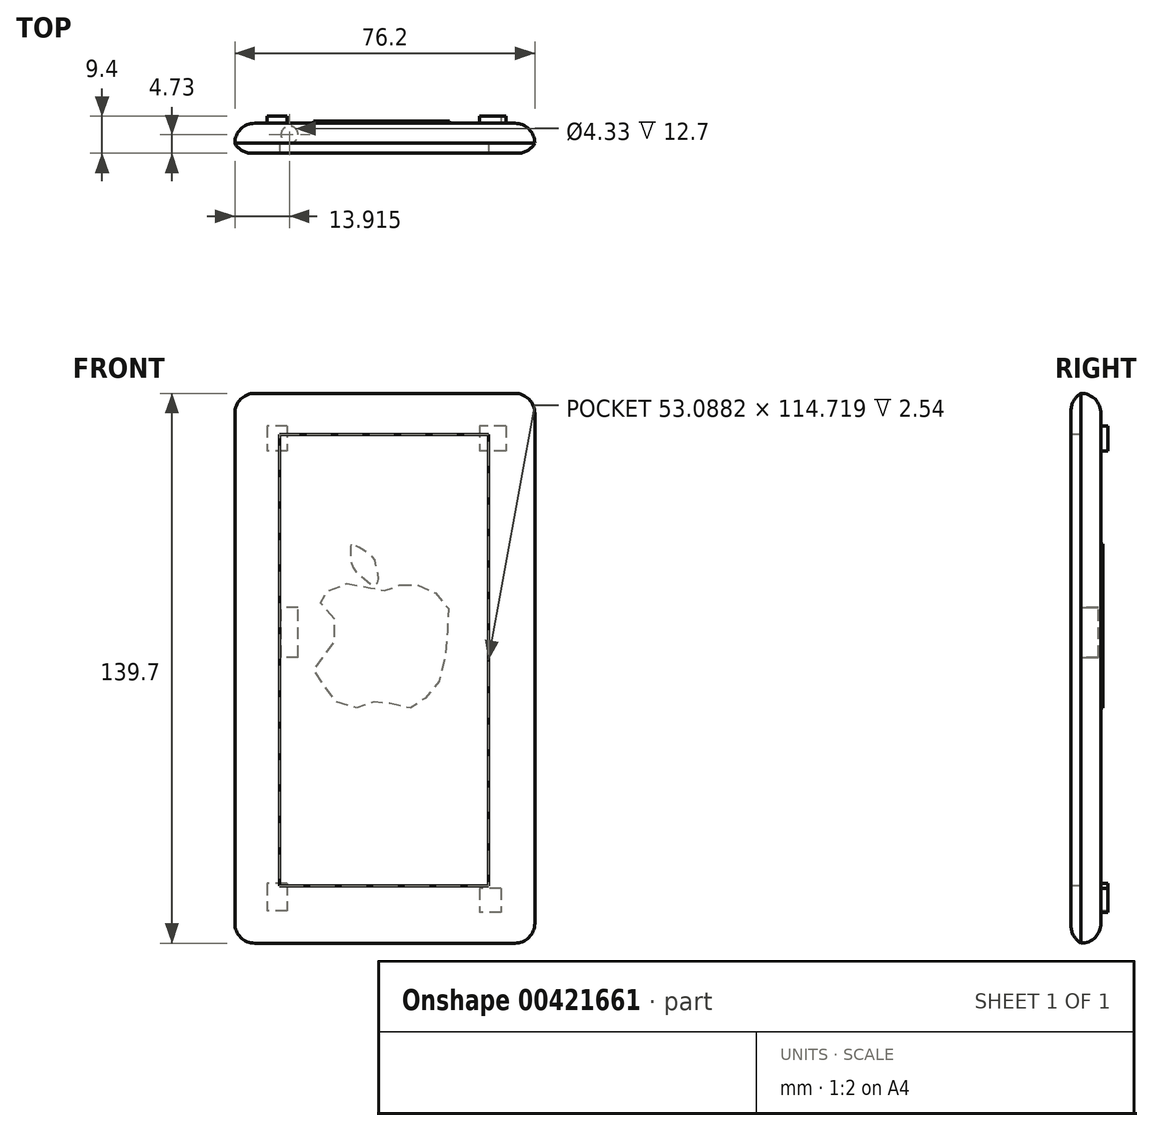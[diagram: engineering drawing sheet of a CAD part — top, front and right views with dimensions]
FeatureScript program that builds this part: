
annotation { "Feature Type Name" : "Feature", "Feature Type Description" : "" }
export const myFeature = defineFeature(function(context is Context, id is Id, definition is map)
    precondition{}
    {
        {
            var Q0;
            Q0=qCreatedBy(makeId("Front.planeOp"),FACE);
            var sketch = newSketch(context, id + "F0", { "sketchPlane" : qUnion([Q0])});
            skLineSegment(sketch, "E0.bottom", {"start": v(-44.86, 54.34) * mm, "end": v(31.34, 54.34) * mm});
            skLineSegment(sketch, "E0.top", {"start": v(-44.86, -85.36) * mm, "end": v(31.34, -85.36) * mm});
            skLineSegment(sketch, "E0.left", {"start": v(-44.86, 54.34) * mm, "end": v(-44.86, -85.36) * mm});
            skLineSegment(sketch, "E0.right", {"start": v(31.34, 54.34) * mm, "end": v(31.34, -85.36) * mm});
            skSolve(sketch);
        }
        {
            var Q0;
            Q0=makeQuery(id+"F0.imprint","IMPRINT",FACE,{"disambiguationData":[TD([[makeQuery(id+"F0.imprint","IMPRINT",EDGE,{"derivedFrom":sQuery(id+"F0.wireOp",EDGE,"E0.bottom")}),-1.0]])]});
            extrude(context, id + "F1", {"entities" : qUnion([Q0]), "depth" : 7.62 * mm});
        }
        {
            var Q0;
            Q0=makeQuery(id+"F1.opExtrude","SWEPT_EDGE",EDGE,{"disambiguationData":[OSD([sQuery(id+"F0.wireOp",EDGE,"E0.bottom"),sQuery(id+"F0.wireOp",EDGE,"E0.left")])]});
            fillet(context, id + "F2", {"entities" : qUnion([Q0]), "radius" : 5.08 * mm, "tangentPropagation" : true, "allowEdgeOverflow" : false});
        }
        {
            var Q0;
            Q0=makeQuery(id+"F1.opExtrude","SWEPT_EDGE",EDGE,{"disambiguationData":[OSD([sQuery(id+"F0.wireOp",EDGE,"E0.top"),sQuery(id+"F0.wireOp",EDGE,"E0.right")])]});
            fillet(context, id + "F3", {"entities" : qUnion([Q0]), "radius" : 5.08 * mm, "tangentPropagation" : true, "allowEdgeOverflow" : false});
        }
        {
            var Q0;
            Q0=makeQuery(id+"F1.opExtrude","SWEPT_EDGE",EDGE,{"disambiguationData":[OSD([sQuery(id+"F0.wireOp",EDGE,"E0.bottom"),sQuery(id+"F0.wireOp",EDGE,"E0.right")])]});
            fillet(context, id + "F4", {"entities" : qUnion([Q0]), "radius" : 5.08 * mm, "tangentPropagation" : true, "allowEdgeOverflow" : false});
        }
        {
            var Q0;
            Q0=makeQuery(id+"F1.opExtrude","SWEPT_EDGE",EDGE,{"disambiguationData":[OSD([sQuery(id+"F0.wireOp",EDGE,"E0.top"),sQuery(id+"F0.wireOp",EDGE,"E0.left")])]});
            fillet(context, id + "F5", {"entities" : qUnion([Q0]), "radius" : 5.08 * mm, "tangentPropagation" : true, "allowEdgeOverflow" : false});
        }
        {
            var Q0;
            Q0=makeQuery(id+"F1.opExtrude","CAP_EDGE",EDGE,{"disambiguationData":[OSD([sQuery(id+"F0.wireOp",EDGE,"E0.left")])],"isStart":true});
            fillet(context, id + "F6", {"entities" : qUnion([Q0]), "radius" : 5.08 * mm, "tangentPropagation" : true, "allowEdgeOverflow" : false});
        }
        {
            var Q0;
            Q0=makeQuery(id+"F1.opExtrude","CAP_FACE",FACE,{"disambiguationData":[OSD([sQuery(id+"F0.wireOp",EDGE,"E0.bottom"),sQuery(id+"F0.wireOp",EDGE,"E0.top"),sQuery(id+"F0.wireOp",EDGE,"E0.left"),sQuery(id+"F0.wireOp",EDGE,"E0.right")])],"isStart":false});
            var sketch = newSketch(context, id + "F7", { "sketchPlane" : qUnion([Q0])});
            skLineSegment(sketch, "E1.bottom", {"start": v(-33.56, 43.93) * mm, "end": v(19.53, 43.93) * mm});
            skLineSegment(sketch, "E1.top", {"start": v(-33.56, -70.79) * mm, "end": v(19.53, -70.79) * mm});
            skLineSegment(sketch, "E1.left", {"start": v(-33.56, 43.93) * mm, "end": v(-33.56, -70.79) * mm});
            skLineSegment(sketch, "E1.right", {"start": v(19.53, 43.93) * mm, "end": v(19.53, -70.79) * mm});
            skSolve(sketch);
        }
        {
            var Q0;
            Q0=makeQuery(id+"F1.opExtrude","CAP_FACE",FACE,{"disambiguationData":[OSD([sQuery(id+"F0.wireOp",EDGE,"E0.bottom"),sQuery(id+"F0.wireOp",EDGE,"E0.top"),sQuery(id+"F0.wireOp",EDGE,"E0.left"),sQuery(id+"F0.wireOp",EDGE,"E0.right")])],"isStart":true});
            var sketch = newSketch(context, id + "F8", { "sketchPlane" : qUnion([Q0])});
            skLineSegment(sketch, "E2.bottom", {"start": v(-24, 46.07) * mm, "end": v(-17.29, 46.07) * mm});
            skLineSegment(sketch, "E2.top", {"start": v(-24, 39.66) * mm, "end": v(-17.29, 39.66) * mm});
            skLineSegment(sketch, "E2.left", {"start": v(-24, 46.07) * mm, "end": v(-24, 39.66) * mm});
            skLineSegment(sketch, "E2.right", {"start": v(-17.29, 46.07) * mm, "end": v(-17.29, 39.66) * mm});
            skLineSegment(sketch, "E3.bottom", {"start": v(31.53, 46.07) * mm, "end": v(36.71, 46.07) * mm});
            skLineSegment(sketch, "E3.top", {"start": v(31.53, 39.66) * mm, "end": v(36.71, 39.66) * mm});
            skLineSegment(sketch, "E3.left", {"start": v(31.53, 46.07) * mm, "end": v(31.53, 39.66) * mm});
            skLineSegment(sketch, "E3.right", {"start": v(36.71, 46.07) * mm, "end": v(36.71, 39.66) * mm});
            skLineSegment(sketch, "E4.bottom", {"start": v(-22.78, -71.4) * mm, "end": v(-17.29, -71.4) * mm});
            skLineSegment(sketch, "E4.top", {"start": v(-22.78, -77.5) * mm, "end": v(-17.29, -77.5) * mm});
            skLineSegment(sketch, "E4.left", {"start": v(-22.78, -71.4) * mm, "end": v(-22.78, -77.5) * mm});
            skLineSegment(sketch, "E4.right", {"start": v(-17.29, -71.4) * mm, "end": v(-17.29, -77.5) * mm});
            skLineSegment(sketch, "E5.bottom", {"start": v(31.53, -70.18) * mm, "end": v(36.71, -70.18) * mm});
            skLineSegment(sketch, "E5.top", {"start": v(31.53, -77.2) * mm, "end": v(36.71, -77.2) * mm});
            skLineSegment(sketch, "E5.left", {"start": v(31.53, -70.18) * mm, "end": v(31.53, -77.2) * mm});
            skLineSegment(sketch, "E5.right", {"start": v(36.71, -70.18) * mm, "end": v(36.71, -77.2) * mm});
            skSolve(sketch);
        }
        {
            var Q0;
            Q0 = qSketchRegion(id + "F8", true);
            extrude(context, id + "F9", {"entities" : qUnion([Q0]), "operationType" : NewBodyOperationType.ADD, "depth" : 1.78 * mm});
        }
        {
            var Q0;
            Q0=makeQuery(id+"F7.imprint","IMPRINT",FACE,{"disambiguationData":[TD([[makeQuery(id+"F7.imprint","IMPRINT",EDGE,{"derivedFrom":sQuery(id+"F7.wireOp",EDGE,"E1.bottom")}),-1.0]])]});
            extrude(context, id + "F10", {"entities" : qUnion([Q0]), "operationType" : NewBodyOperationType.REMOVE, "oppositeDirection" : true, "depth" : 2.54 * mm});
        }
        {
            var Q0;
            Q0=makeQuery(id+"F10.boolean.opBoolean","COPY",FACE,{"derivedFrom":makeQuery(id+"F10.opExtrude","CAP_FACE",FACE,{"disambiguationData":[OSD([sQuery(id+"F7.wireOp",EDGE,"E1.bottom"),sQuery(id+"F7.wireOp",EDGE,"E1.top"),sQuery(id+"F7.wireOp",EDGE,"E1.left"),sQuery(id+"F7.wireOp",EDGE,"E1.right")])],"isStart":false})});
            var sketch = newSketch(context, id + "F11", { "sketchPlane" : qUnion([Q0])});
            skLineSegment(sketch, "E6.bottom", {"start": v(-33.56, 43.93) * mm, "end": v(19.53, 43.93) * mm});
            skLineSegment(sketch, "E6.top", {"start": v(-33.56, -70.79) * mm, "end": v(19.53, -70.79) * mm});
            skLineSegment(sketch, "E6.left", {"start": v(-33.56, 43.93) * mm, "end": v(-33.56, -70.79) * mm});
            skLineSegment(sketch, "E6.right", {"start": v(19.53, 43.93) * mm, "end": v(19.53, -70.79) * mm});
            skSolve(sketch);
        }
        {
            var Q0;
            Q0 = qSketchRegion(id + "F11", true);
            extrude(context, id + "F12", {"entities" : qUnion([Q0]), "depth" : 2.54 * mm});
        }
        {
            var Q0;
            Q0=makeQuery(id+"F1.opExtrude","CAP_FACE",FACE,{"disambiguationData":[OSD([sQuery(id+"F0.wireOp",EDGE,"E0.bottom"),sQuery(id+"F0.wireOp",EDGE,"E0.top"),sQuery(id+"F0.wireOp",EDGE,"E0.left"),sQuery(id+"F0.wireOp",EDGE,"E0.right")])],"isStart":true});
            var sketch = newSketch(context, id + "F13", { "sketchPlane" : qUnion([Q0])});
            skPoint(sketch, "E7.8.internal.orphan", {"position": v(0, -25.6) * mm});
            skFitSpline(sketch, "E8", {"points": [v(15.28, 16) * mm, v(15.52, 14.86) * mm, v(14.93, 10.25) * mm, v(12.2, 7.4) * mm, v(10.08, 5.87) * mm, v(8.46, 6.4) * mm, v(8.93, 10.3) * mm, v(9.49, 12.37) * mm, v(12.56, 14.74) * mm, v(15.28, 16) * mm]});
            skFitSpline(sketch, "E9", {"points": [v(2.98, 5.63) * mm, v(0, 5.99) * mm, v(-4.12, 4.69) * mm, v(-7.67, 2.32) * mm, v(-9.68, -1.7) * mm, v(-8.81, -8.03) * mm, v(-8.26, -15.54) * mm, v(-5.77, -20.63) * mm, v(-2.46, -24.06) * mm, v(0, -25.6) * mm, v(4.87, -24.65) * mm, v(7, -24.06) * mm, v(10.67, -24.3) * mm, v(14.1, -25.6) * mm, v(18.6, -24.3) * mm, v(21.55, -21.1) * mm, v(23.92, -16.96) * mm, v(24.89, -15.19) * mm, v(22.97, -13.18) * mm, v(20.01, -9.98) * mm, v(19.19, -4.66) * mm, v(21.43, 0) * mm, v(23.8, 1.96) * mm, v(20.49, 4.57) * mm, v(15.87, 6.1) * mm, v(10.08, 4.8) * mm, v(8.07, 4.1) * mm, v(5.35, 4.69) * mm, v(2.98, 5.63) * mm]});
            skSolve(sketch);
        }
        {
            var Q0;
            Q0=makeQuery(id+"F1.opExtrude","CAP_EDGE",EDGE,{"disambiguationData":[OSD([sQuery(id+"F0.wireOp",EDGE,"E0.left")])],"isStart":false});
            fillet(context, id + "F14", {"entities" : qUnion([Q0]), "radius" : 5.08 * mm, "tangentPropagation" : true, "allowEdgeOverflow" : false});
        }
        {
            var Q0;
            Q0=qCreatedBy(makeId("Top.planeOp"),FACE);
            var sketch = newSketch(context, id + "F15", { "sketchPlane" : qUnion([Q0])});
            skCircle(sketch, "E10", {"center": v(-30.94, -2.9) * mm, "radius": 2.17 * mm});
            skSolve(sketch);
        }
        {
            var Q0;
            Q0 = qSketchRegion(id + "F15", true);
            extrude(context, id + "F16", {"entities" : qUnion([Q0]), "operationType" : NewBodyOperationType.REMOVE, "oppositeDirection" : true, "depth" : 12.7 * mm});
        }
        {
            var Q0;
            Q0=makeQuery(id+"F13.imprint","IMPRINT",FACE,{"disambiguationData":[TD([[makeQuery(id+"F13.imprint","IMPRINT",EDGE,{"derivedFrom":sQuery(id+"F13.wireOp",EDGE,"E9")}),1.0]])]});
            var Q1;
            Q1=makeQuery(id+"F13.imprint","IMPRINT",FACE,{"disambiguationData":[TD([[makeQuery(id+"F13.imprint","IMPRINT",EDGE,{"derivedFrom":sQuery(id+"F13.wireOp",EDGE,"E8")}),-1.0]])]});
            extrude(context, id + "F17", {"entities" : qUnion([Q0, Q1]), "operationType" : NewBodyOperationType.ADD, "depth" : 0.5 * mm});
        }
    });
